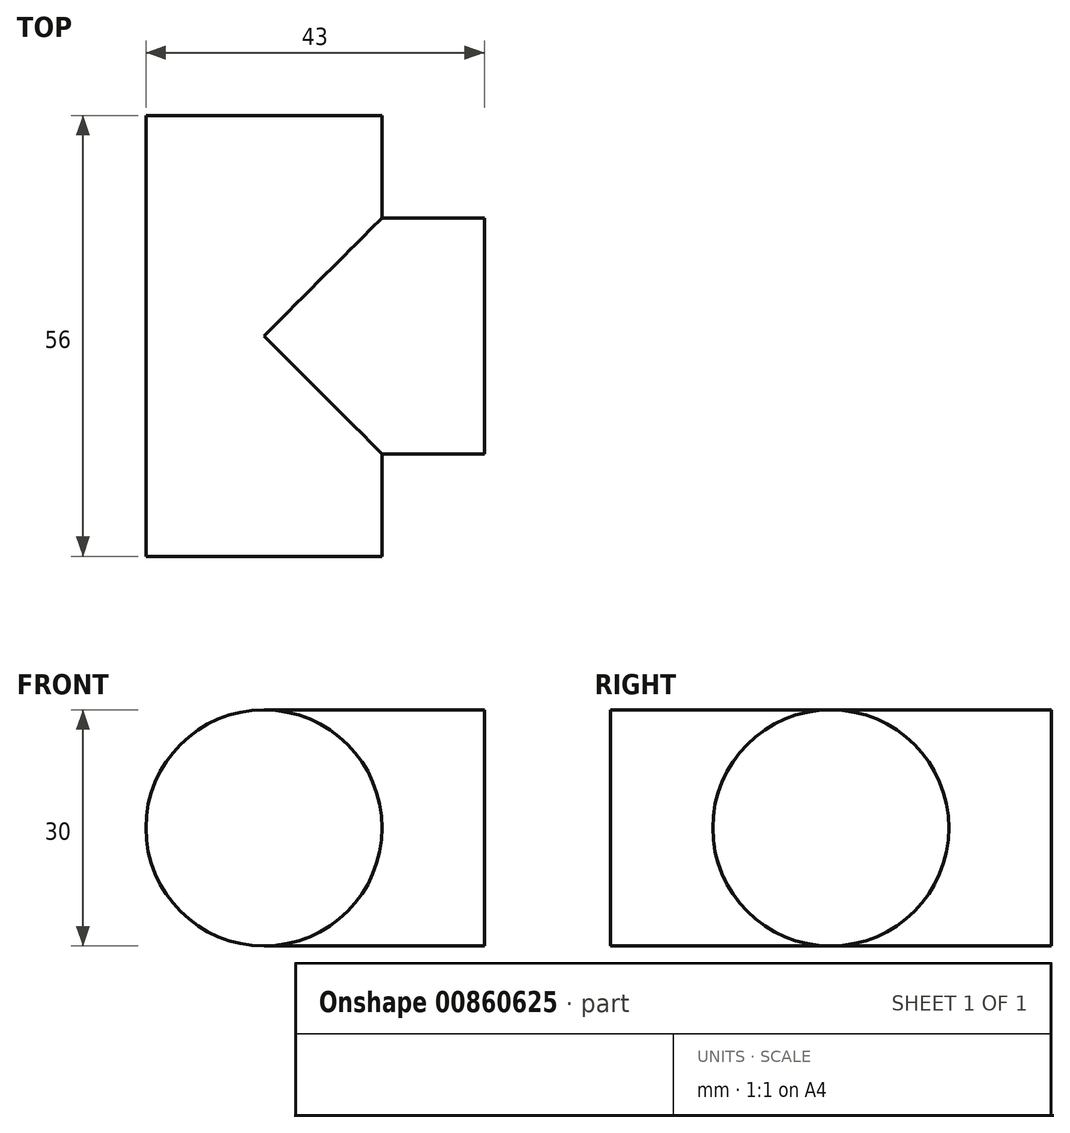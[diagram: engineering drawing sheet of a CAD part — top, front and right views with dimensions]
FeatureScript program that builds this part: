
annotation { "Feature Type Name" : "Feature", "Feature Type Description" : "" }
export const myFeature = defineFeature(function(context is Context, id is Id, definition is map)
    precondition{}
    {
        {
            var Q0;
            Q0=qCreatedBy(makeId("Front.planeOp"),FACE);
            var sketch = newSketch(context, id + "F0", { "sketchPlane" : qUnion([Q0])});
            skCircle(sketch, "E0", {"center": v(0, 0) * mm, "radius": 15 * mm});
            skSolve(sketch);
        }
        {
            var Q0;
            Q0=makeQuery(id+"F0.imprint","IMPRINT",FACE,{"disambiguationData":[TD([[makeQuery(id+"F0.imprint","IMPRINT",EDGE,{"derivedFrom":sQuery(id+"F0.wireOp",EDGE,"E0")}),1.0]])]});
            var Q1;
            Q1=sQuery(id+"F0.wireOp",EDGE,"E0");
            extrude(context, id + "F1", {"entities" : qUnion([Q0]), "surfaceEntities" : qUnion([Q1]), "depth" : 28 * mm, "offsetDistance" : 25.4 * mm});
        }
        {
            var Q0;
            Q0=makeQuery(id+"F1.opExtrude","CAP_FACE",FACE,{"disambiguationData":[OSD([sQuery(id+"F0.wireOp",EDGE,"E0")])],"isStart":true});
            extrude(context, id + "F2", {"entities" : qUnion([Q0]), "operationType" : NewBodyOperationType.ADD, "depth" : 28 * mm, "offsetDistance" : 25.4 * mm});
        }
        {
            var Q0;
            Q0=qCreatedBy(makeId("Right.planeOp"),FACE);
            var sketch = newSketch(context, id + "F3", { "sketchPlane" : qUnion([Q0])});
            skCircle(sketch, "E1", {"center": v(0, 0) * mm, "radius": 15 * mm});
            skSolve(sketch);
        }
        {
            var Q0;
            Q0=makeQuery(id+"F3.imprint","IMPRINT",FACE,{"disambiguationData":[TD([[makeQuery(id+"F3.imprint","IMPRINT",EDGE,{"derivedFrom":sQuery(id+"F3.wireOp",EDGE,"E1")}),1.0]])]});
            var Q1;
            Q1=sQuery(id+"F3.wireOp",EDGE,"E1");
            extrude(context, id + "F4", {"entities" : qUnion([Q0]), "operationType" : NewBodyOperationType.ADD, "surfaceEntities" : qUnion([Q1]), "depth" : 28 * mm, "offsetDistance" : 25.4 * mm});
        }
    });
